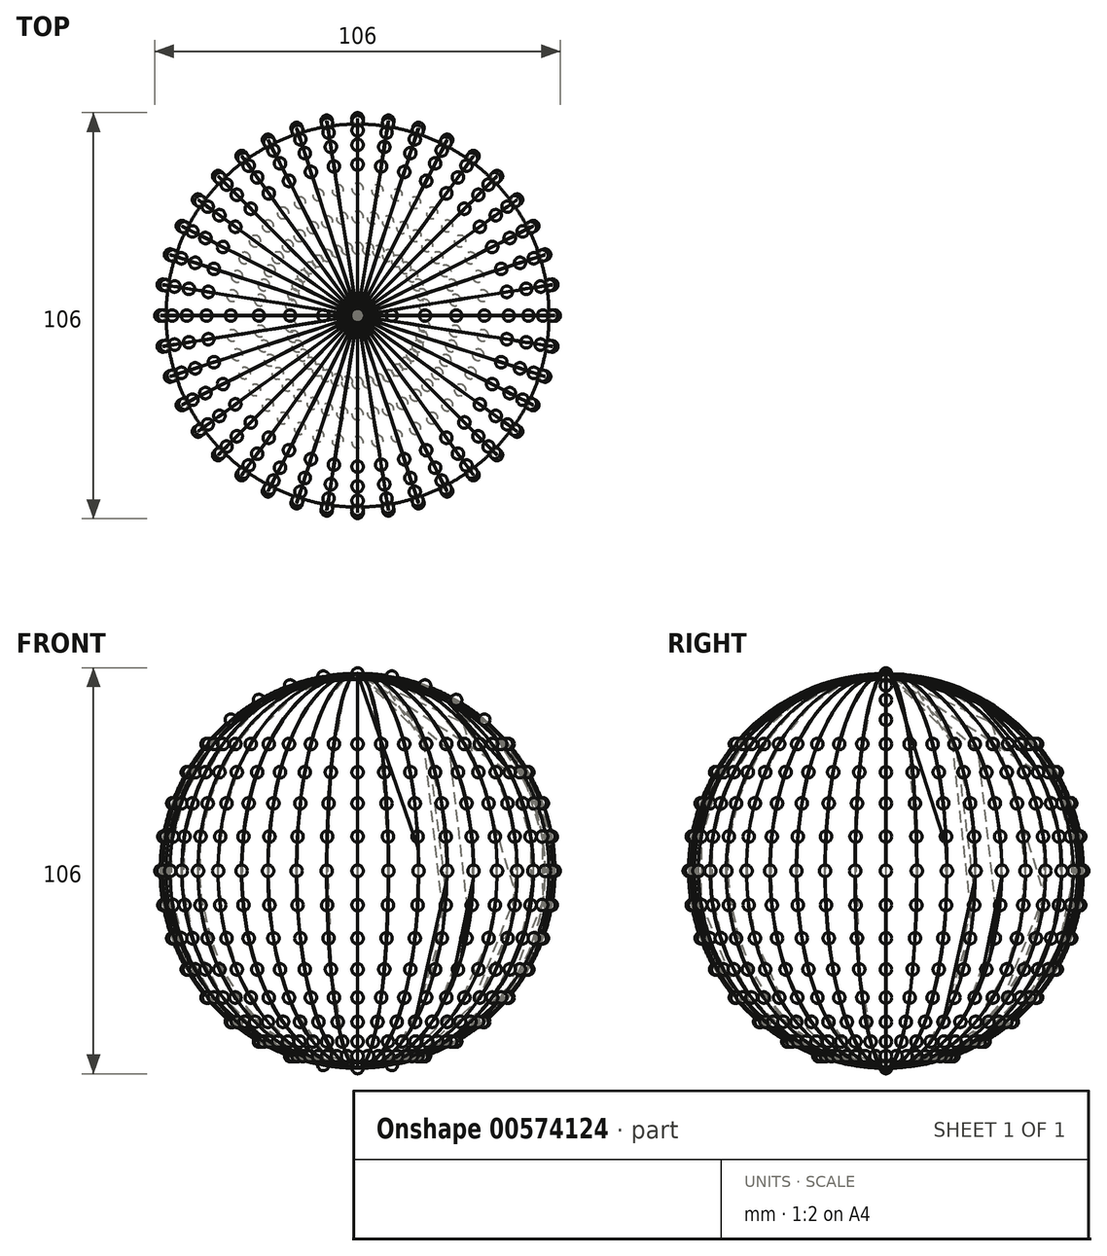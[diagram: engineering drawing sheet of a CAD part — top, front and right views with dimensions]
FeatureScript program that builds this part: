
annotation { "Feature Type Name" : "Feature", "Feature Type Description" : "" }
export const myFeature = defineFeature(function(context is Context, id is Id, definition is map)
    precondition{}
    {
        {
            var Q0;
            Q0=qCreatedBy(makeId("Front.planeOp"),FACE);
            var sketch = newSketch(context, id + "F0", { "sketchPlane" : qUnion([Q0])});
            skArc(sketch, "E0", {"start": v(0, -50) * mm, "mid": v(50, 0) * mm, "end": v(0, 50) * mm});
            skCircle(sketch, "E1", {"center": v(0, 0) * mm, "radius": 51.5 * mm});
            skLineSegment(sketch, "E2", {"start": v(0, 50) * mm, "end": v(0, -50) * mm});
            skSolve(sketch);
        }
        {
            var Q0;
            Q0=makeQuery(id+"F0.imprint","IMPRINT",FACE,{"disambiguationData":[TD([[makeQuery(id+"F0.imprint","IMPRINT",EDGE,{"derivedFrom":sQuery(id+"F0.wireOp",EDGE,"E0")}),1.0]])]});
            var Q1;
            Q1=sQuery(id+"F0.wireOp",EDGE,"E2");
            revolve(context, id + "F1", {"entities" : qUnion([Q0]), "axis" : qUnion([Q1]), "revolveType" : RevolveType.FULL});
        }
        {
            var Q0;
            Q0=qCreatedBy(makeId("Right.planeOp"),FACE);
            var sketch = newSketch(context, id + "F2", { "sketchPlane" : qUnion([Q0])});
            skLineSegment(sketch, "E3.0", {"start": v(0, -51.5) * mm, "end": v(0, 51.5) * mm, "construction": true});
            skCircle(sketch, "E4", {"center": v(0, 51.5) * mm, "radius": 0.05 * mm});
            skSolve(sketch);
        }
        {
            var Q0;
            Q0=makeQuery(id+"F2.imprint","IMPRINT",FACE,{"disambiguationData":[TD([[makeQuery(id+"F2.imprint","IMPRINT",EDGE,{"derivedFrom":sQuery(id+"F2.wireOp",EDGE,"E4")}),1.0]])]});
            var Q1;
            Q1=sQuery(id+"F0.wireOp",EDGE,"E1");
            sweep(context, id + "F3", {"profiles" : qUnion([Q0]), "path" : qUnion([Q1])});
        }
        {
            var Q0;
            Q0=qCreatedBy(makeId("Front.planeOp"),FACE);
            var sketch = newSketch(context, id + "F4", { "sketchPlane" : qUnion([Q0])});
            skArc(sketch, "E5", {"start": v(0, 50) * mm, "mid": v(1.5, 51.5) * mm, "end": v(0, 53) * mm});
            skLineSegment(sketch, "E6", {"start": v(0, 53) * mm, "end": v(0, 50) * mm});
            skSolve(sketch);
        }
        {
            var Q0;
            Q0 = qSketchRegion(id + "F4", true);
            var Q1;
            Q1=sQuery(id+"F4.wireOp",EDGE,"E6");
            revolve(context, id + "F5", {"entities" : qUnion([Q0]), "axis" : qUnion([Q1]), "revolveType" : RevolveType.FULL});
        }
        {
            var Q0;
            Q0=makeQuery(id+"F5.opRevolve","SWEPT_BODY",BODY,{"disambiguationData":[OSD([sQuery(id+"F4.wireOp",EDGE,"E5"),sQuery(id+"F4.wireOp",EDGE,"E6")])]});
            var Q1;
            Q1=sQuery(id+"F0.wireOp",EDGE,"E1");
            circularPattern(context, id + "F6", {"entities" : qUnion([Q0]), "axis" : qUnion([Q1]), "angle" : 360 * degree, "instanceCount" : 36, "equalSpace" : true});
        }
        {
            var Q0;
            Q0=makeQuery(id+"F6.opPattern","COPY",BODY,{"derivedFrom":makeQuery(id+"F5.opRevolve","SWEPT_BODY",BODY,{"disambiguationData":[OSD([sQuery(id+"F4.wireOp",EDGE,"E5"),sQuery(id+"F4.wireOp",EDGE,"E6")])]}),"instanceName":"27"});
            var Q1;
            Q1=makeQuery(id+"F3.opSweep","SWEPT_BODY",BODY,{"disambiguationData":[OSD([sQuery(id+"F0.wireOp",EDGE,"E1"),sQuery(id+"F2.wireOp",EDGE,"E4")])]});
            var Q2;
            Q2=makeQuery(id+"F6.opPattern","COPY",BODY,{"derivedFrom":makeQuery(id+"F5.opRevolve","SWEPT_BODY",BODY,{"disambiguationData":[OSD([sQuery(id+"F4.wireOp",EDGE,"E5"),sQuery(id+"F4.wireOp",EDGE,"E6")])]}),"instanceName":"26"});
            var Q3;
            Q3=makeQuery(id+"F6.opPattern","COPY",BODY,{"derivedFrom":makeQuery(id+"F5.opRevolve","SWEPT_BODY",BODY,{"disambiguationData":[OSD([sQuery(id+"F4.wireOp",EDGE,"E5"),sQuery(id+"F4.wireOp",EDGE,"E6")])]}),"instanceName":"25"});
            var Q4;
            Q4=makeQuery(id+"F6.opPattern","COPY",BODY,{"derivedFrom":makeQuery(id+"F5.opRevolve","SWEPT_BODY",BODY,{"disambiguationData":[OSD([sQuery(id+"F4.wireOp",EDGE,"E5"),sQuery(id+"F4.wireOp",EDGE,"E6")])]}),"instanceName":"28"});
            var Q5;
            Q5=makeQuery(id+"F6.opPattern","COPY",BODY,{"derivedFrom":makeQuery(id+"F5.opRevolve","SWEPT_BODY",BODY,{"disambiguationData":[OSD([sQuery(id+"F4.wireOp",EDGE,"E5"),sQuery(id+"F4.wireOp",EDGE,"E6")])]}),"instanceName":"29"});
            var Q6;
            Q6=makeQuery(id+"F6.opPattern","COPY",BODY,{"derivedFrom":makeQuery(id+"F5.opRevolve","SWEPT_BODY",BODY,{"disambiguationData":[OSD([sQuery(id+"F4.wireOp",EDGE,"E5"),sQuery(id+"F4.wireOp",EDGE,"E6")])]}),"instanceName":"30"});
            var Q7;
            Q7=makeQuery(id+"F6.opPattern","COPY",BODY,{"derivedFrom":makeQuery(id+"F5.opRevolve","SWEPT_BODY",BODY,{"disambiguationData":[OSD([sQuery(id+"F4.wireOp",EDGE,"E5"),sQuery(id+"F4.wireOp",EDGE,"E6")])]}),"instanceName":"31"});
            var Q8;
            Q8=makeQuery(id+"F6.opPattern","COPY",BODY,{"derivedFrom":makeQuery(id+"F5.opRevolve","SWEPT_BODY",BODY,{"disambiguationData":[OSD([sQuery(id+"F4.wireOp",EDGE,"E5"),sQuery(id+"F4.wireOp",EDGE,"E6")])]}),"instanceName":"24"});
            var Q9;
            Q9=makeQuery(id+"F6.opPattern","COPY",BODY,{"derivedFrom":makeQuery(id+"F5.opRevolve","SWEPT_BODY",BODY,{"disambiguationData":[OSD([sQuery(id+"F4.wireOp",EDGE,"E5"),sQuery(id+"F4.wireOp",EDGE,"E6")])]}),"instanceName":"23"});
            var Q10;
            Q10=makeQuery(id+"F6.opPattern","COPY",BODY,{"derivedFrom":makeQuery(id+"F5.opRevolve","SWEPT_BODY",BODY,{"disambiguationData":[OSD([sQuery(id+"F4.wireOp",EDGE,"E5"),sQuery(id+"F4.wireOp",EDGE,"E6")])]}),"instanceName":"22"});
            var Q11;
            Q11=makeQuery(id+"F6.opPattern","COPY",BODY,{"derivedFrom":makeQuery(id+"F5.opRevolve","SWEPT_BODY",BODY,{"disambiguationData":[OSD([sQuery(id+"F4.wireOp",EDGE,"E5"),sQuery(id+"F4.wireOp",EDGE,"E6")])]}),"instanceName":"21"});
            var Q12;
            Q12=makeQuery(id+"F6.opPattern","COPY",BODY,{"derivedFrom":makeQuery(id+"F5.opRevolve","SWEPT_BODY",BODY,{"disambiguationData":[OSD([sQuery(id+"F4.wireOp",EDGE,"E5"),sQuery(id+"F4.wireOp",EDGE,"E6")])]}),"instanceName":"20"});
            var Q13;
            Q13=sQuery(id+"F2.wireOp",EDGE,"E3.0");
            circularPattern(context, id + "F7", {"entities" : qUnion([Q0, Q1, Q2, Q3, Q4, Q5, Q6, Q7, Q8, Q9, Q10, Q11, Q12]), "axis" : qUnion([Q13]), "angle" : 360 * degree, "instanceCount" : 40, "equalSpace" : true});
        }
        {
            var Q0;
            Q0=qCreatedBy(makeId("Front.planeOp"),FACE);
            var sketch = newSketch(context, id + "F8", { "sketchPlane" : qUnion([Q0])});
            skCircle(sketch, "E7", {"center": v(0, 0) * mm, "radius": 1.5 * mm, "construction": true});
            skCircle(sketch, "E8", {"center": v(7.93, -8.94) * mm, "radius": 1.5 * mm, "construction": true});
            skCircle(sketch, "E9", {"center": v(7.93, 8.94) * mm, "radius": 1.5 * mm, "construction": true});
            skLineSegment(sketch, "E10", {"start": v(0, 0) * mm, "end": v(7.93, 8.94) * mm, "construction": true});
            skLineSegment(sketch, "E11", {"start": v(0, 0) * mm, "end": v(7.93, -8.94) * mm, "construction": true});
            skCircle(sketch, "E12", {"center": v(-7.93, -8.94) * mm, "radius": 1.5 * mm});
            skCircle(sketch, "E13", {"center": v(-7.93, 8.94) * mm, "radius": 1.5 * mm});
            skLineSegment(sketch, "E14", {"start": v(0, 0) * mm, "end": v(-7.93, 8.94) * mm, "construction": true});
            skCircle(sketch, "E15", {"center": v(-15.67, 8.94) * mm, "radius": 1.5 * mm});
            skCircle(sketch, "E16", {"center": v(-14.95, 17.61) * mm, "radius": 1.5 * mm});
            skCircle(sketch, "E17", {"center": v(-7.57, 17.61) * mm, "radius": 1.5 * mm});
            skCircle(sketch, "E18", {"center": v(-6.98, 25.75) * mm, "radius": 1.5 * mm});
            skCircle(sketch, "E19", {"center": v(-13.78, 25.75) * mm, "radius": 1.5 * mm});
            skCircle(sketch, "E20", {"center": v(-6.17, 33.1) * mm, "radius": 1.5 * mm});
            skCircle(sketch, "E21", {"center": v(-12.2, 33.1) * mm, "radius": 1.5 * mm});
            skCircle(sketch, "E22", {"center": v(-17.91, 33.1) * mm, "radius": 1.5 * mm});
            skCircle(sketch, "E23", {"center": v(-23.19, 33.1) * mm, "radius": 1.5 * mm});
            skCircle(sketch, "E24", {"center": v(-27.9, 33.1) * mm, "radius": 1.5 * mm});
            skCircle(sketch, "E25", {"center": v(-31.92, 33.1) * mm, "radius": 1.5 * mm});
            skCircle(sketch, "E26", {"center": v(-35.15, 33.1) * mm, "radius": 1.5 * mm});
            skCircle(sketch, "E27", {"center": v(-36.08, 25.75) * mm, "radius": 1.5 * mm});
            skCircle(sketch, "E28", {"center": v(-31.54, 25.75) * mm, "radius": 1.5 * mm});
            skCircle(sketch, "E29", {"center": v(-26.22, 25.75) * mm, "radius": 1.5 * mm});
            skLineSegment(sketch, "E30.0", {"start": v(0, -51.5) * mm, "end": v(0, 51.5) * mm});
            skCircle(sketch, "E31", {"center": v(6.17, 33.1) * mm, "radius": 1.5 * mm});
            skCircle(sketch, "E32", {"center": v(6.98, 25.75) * mm, "radius": 1.5 * mm});
            skCircle(sketch, "E33", {"center": v(0, 25.75) * mm, "radius": 1.5 * mm});
            skCircle(sketch, "E34", {"center": v(17.91, 33.1) * mm, "radius": 1.5 * mm});
            skCircle(sketch, "E35", {"center": v(27.9, 33.1) * mm, "radius": 1.5 * mm});
            skCircle(sketch, "E36", {"center": v(35.15, 33.1) * mm, "radius": 1.5 * mm});
            skCircle(sketch, "E37", {"center": v(0, 0) * mm, "radius": 50 * mm});
            skCircle(sketch, "E38", {"center": v(39.74, 25.75) * mm, "radius": 1.5 * mm});
            skCircle(sketch, "E39", {"center": v(31.54, 25.75) * mm, "radius": 1.5 * mm});
            skCircle(sketch, "E40", {"center": v(20.25, 25.75) * mm, "radius": 1.5 * mm});
            skCircle(sketch, "E41", {"center": v(7.57, 17.61) * mm, "radius": 1.5 * mm});
            skCircle(sketch, "E42", {"center": v(14.95, 17.61) * mm, "radius": 1.5 * mm});
            skCircle(sketch, "E43", {"center": v(21.97, 17.61) * mm, "radius": 1.5 * mm});
            skCircle(sketch, "E44", {"center": v(34.22, 17.61) * mm, "radius": 1.5 * mm});
            skCircle(sketch, "E45", {"center": v(39.15, 17.61) * mm, "radius": 1.5 * mm});
            skCircle(sketch, "E46", {"center": v(46.03, 17.61) * mm, "radius": 1.5 * mm});
            skCircle(sketch, "E47", {"center": v(45.19, 8.94) * mm, "radius": 1.5 * mm});
            skCircle(sketch, "E48", {"center": v(35.86, 8.94) * mm, "radius": 1.5 * mm});
            skCircle(sketch, "E49", {"center": v(15.67, 8.94) * mm, "radius": 1.5 * mm});
            skCircle(sketch, "E50", {"center": v(23.38, 0) * mm, "radius": 1.5 * mm});
            skCircle(sketch, "E51", {"center": v(30.27, 0) * mm, "radius": 1.5 * mm});
            skCircle(sketch, "E52", {"center": v(48.98, 0) * mm, "radius": 1.5 * mm});
            skCircle(sketch, "E53", {"center": v(48.24, -8.94) * mm, "radius": 1.5 * mm});
            skCircle(sketch, "E54", {"center": v(41.03, -8.94) * mm, "radius": 1.5 * mm});
            skCircle(sketch, "E55", {"center": v(29.81, -8.94) * mm, "radius": 1.5 * mm});
            skCircle(sketch, "E56", {"center": v(0, -8.94) * mm, "radius": 1.5 * mm});
            skCircle(sketch, "E57", {"center": v(-15.67, -8.94) * mm, "radius": 1.5 * mm});
            skCircle(sketch, "E58", {"center": v(-28.45, 17.61) * mm, "radius": 1.5 * mm});
            skCircle(sketch, "E59", {"center": v(-15.91, 0) * mm, "radius": 1.5 * mm});
            skCircle(sketch, "E60", {"center": v(-45.89, 0) * mm, "radius": 1.5 * mm});
            skCircle(sketch, "E61", {"center": v(-45.19, 8.94) * mm, "radius": 1.5 * mm});
            skCircle(sketch, "E62", {"center": v(-46.03, -17.61) * mm, "radius": 1.5 * mm});
            skCircle(sketch, "E63", {"center": v(-43.12, -17.61) * mm, "radius": 1.5 * mm});
            skCircle(sketch, "E64", {"center": v(-21.97, -17.61) * mm, "radius": 1.5 * mm});
            skCircle(sketch, "E65", {"center": v(-7.57, -17.61) * mm, "radius": 1.5 * mm});
            skCircle(sketch, "E66", {"center": v(-34.22, -17.61) * mm, "radius": 1.5 * mm});
            skCircle(sketch, "E67", {"center": v(-29.81, -8.94) * mm, "radius": 1.5 * mm});
            skCircle(sketch, "E68", {"center": v(-41.03, -8.94) * mm, "radius": 1.5 * mm});
            skCircle(sketch, "E69", {"center": v(-45.19, -8.94) * mm, "radius": 1.5 * mm});
            skCircle(sketch, "E70", {"center": v(-41.66, 0) * mm, "radius": 1.5 * mm});
            skCircle(sketch, "E71", {"center": v(-36.42, 0) * mm, "radius": 1.5 * mm});
            skCircle(sketch, "E72", {"center": v(-30.27, 0) * mm, "radius": 1.5 * mm});
            skCircle(sketch, "E73", {"center": v(-23.38, 0) * mm, "radius": 1.5 * mm});
            skCircle(sketch, "E74", {"center": v(-23.03, 8.94) * mm, "radius": 1.5 * mm});
            skCircle(sketch, "E75", {"center": v(-29.81, 8.94) * mm, "radius": 1.5 * mm});
            skCircle(sketch, "E76", {"center": v(-41.03, 8.94) * mm, "radius": 1.5 * mm});
            skCircle(sketch, "E77", {"center": v(-42.42, -25.75) * mm, "radius": 1.5 * mm});
            skCircle(sketch, "E78", {"center": v(-39.74, -25.75) * mm, "radius": 1.5 * mm});
            skCircle(sketch, "E79", {"center": v(-26.22, -25.75) * mm, "radius": 1.5 * mm});
            skCircle(sketch, "E80", {"center": v(-6.98, -25.75) * mm, "radius": 1.5 * mm});
            skCircle(sketch, "E81", {"center": v(0, -17.61) * mm, "radius": 1.5 * mm});
            skCircle(sketch, "E82", {"center": v(15.67, -8.94) * mm, "radius": 1.5 * mm});
            skCircle(sketch, "E83", {"center": v(15.91, 0) * mm, "radius": 1.5 * mm});
            skCircle(sketch, "E84", {"center": v(8.06, 0) * mm, "radius": 1.5 * mm});
            skCircle(sketch, "E85", {"center": v(45.89, 0) * mm, "radius": 1.5 * mm});
            skCircle(sketch, "E86", {"center": v(41.66, 0) * mm, "radius": 1.5 * mm});
            skCircle(sketch, "E87", {"center": v(36.42, 0) * mm, "radius": 1.5 * mm});
            skCircle(sketch, "E88", {"center": v(29.81, 8.94) * mm, "radius": 1.5 * mm});
            skCircle(sketch, "E89", {"center": v(23.03, 8.94) * mm, "radius": 1.5 * mm});
            skCircle(sketch, "E90", {"center": v(28.45, 17.61) * mm, "radius": 1.5 * mm});
            skCircle(sketch, "E91", {"center": v(26.22, 25.75) * mm, "radius": 1.5 * mm});
            skCircle(sketch, "E92", {"center": v(23.19, 33.1) * mm, "radius": 1.5 * mm});
            skCircle(sketch, "E93", {"center": v(21.97, -17.61) * mm, "radius": 1.5 * mm});
            skCircle(sketch, "E94", {"center": v(7.57, -17.61) * mm, "radius": 1.5 * mm});
            skCircle(sketch, "E95", {"center": v(0, -25.75) * mm, "radius": 1.5 * mm});
            skCircle(sketch, "E96", {"center": v(6.98, -25.75) * mm, "radius": 1.5 * mm});
            skCircle(sketch, "E97", {"center": v(26.22, -25.75) * mm, "radius": 1.5 * mm});
            skCircle(sketch, "E98", {"center": v(20.25, -25.75) * mm, "radius": 1.5 * mm});
            skCircle(sketch, "E99", {"center": v(13.78, -25.75) * mm, "radius": 1.5 * mm});
            skCircle(sketch, "E100", {"center": v(14.95, -17.61) * mm, "radius": 1.5 * mm});
            skCircle(sketch, "E101", {"center": v(0, 33.1) * mm, "radius": 1.5 * mm});
            skCircle(sketch, "E102", {"center": v(12.2, 33.1) * mm, "radius": 1.5 * mm});
            skCircle(sketch, "E103", {"center": v(13.78, 25.75) * mm, "radius": 1.5 * mm});
            skCircle(sketch, "E104", {"center": v(31.92, 33.1) * mm, "radius": 1.5 * mm});
            skCircle(sketch, "E105", {"center": v(37.52, 33.1) * mm, "radius": 1.5 * mm});
            skCircle(sketch, "E106", {"center": v(36.08, 25.75) * mm, "radius": 1.5 * mm});
            skCircle(sketch, "E107", {"center": v(-20.25, 25.75) * mm, "radius": 1.5 * mm});
            skCircle(sketch, "E108", {"center": v(-21.97, 17.61) * mm, "radius": 1.5 * mm});
            skCircle(sketch, "E109", {"center": v(-34.22, 17.61) * mm, "radius": 1.5 * mm});
            skCircle(sketch, "E110", {"center": v(-39.15, 17.61) * mm, "radius": 1.5 * mm});
            skCircle(sketch, "E111", {"center": v(28.45, -17.61) * mm, "radius": 1.5 * mm});
            skCircle(sketch, "E112", {"center": v(45.19, -8.94) * mm, "radius": 1.5 * mm});
            skCircle(sketch, "E113", {"center": v(34.22, -17.61) * mm, "radius": 1.5 * mm});
            skCircle(sketch, "E114", {"center": v(35.86, -8.94) * mm, "radius": 1.5 * mm});
            skCircle(sketch, "E115", {"center": v(39.15, -17.61) * mm, "radius": 1.5 * mm});
            skCircle(sketch, "E116", {"center": v(43.12, -17.61) * mm, "radius": 1.5 * mm});
            skCircle(sketch, "E117", {"center": v(46.03, -17.61) * mm, "radius": 1.5 * mm});
            skCircle(sketch, "E118", {"center": v(39.74, -25.75) * mm, "radius": 1.5 * mm});
            skCircle(sketch, "E119", {"center": v(42.42, -25.75) * mm, "radius": 1.5 * mm});
            skCircle(sketch, "E120", {"center": v(31.54, -25.75) * mm, "radius": 1.5 * mm});
            skCircle(sketch, "E121", {"center": v(27.9, -33.1) * mm, "radius": 1.5 * mm});
            skCircle(sketch, "E122", {"center": v(31.92, -33.1) * mm, "radius": 1.5 * mm});
            skCircle(sketch, "E123", {"center": v(23.19, -33.1) * mm, "radius": 1.5 * mm});
            skCircle(sketch, "E124", {"center": v(17.91, -33.1) * mm, "radius": 1.5 * mm});
            skCircle(sketch, "E125", {"center": v(12.2, -33.1) * mm, "radius": 1.5 * mm});
            skCircle(sketch, "E126", {"center": v(0, -33.1) * mm, "radius": 1.5 * mm});
            skCircle(sketch, "E127", {"center": v(-12.2, -33.1) * mm, "radius": 1.5 * mm});
            skCircle(sketch, "E128", {"center": v(-17.91, -33.1) * mm, "radius": 1.5 * mm});
            skCircle(sketch, "E129", {"center": v(-31.54, -25.75) * mm, "radius": 1.5 * mm});
            skCircle(sketch, "E130", {"center": v(-36.08, -25.75) * mm, "radius": 1.5 * mm});
            skCircle(sketch, "E131", {"center": v(-37.52, -33.1) * mm, "radius": 1.5 * mm});
            skLineSegment(sketch, "E132", {"start": v(0, 0) * mm, "end": v(-7.93, -8.94) * mm, "construction": true});
            skSolve(sketch);
        }
        {
            var Q0;
            Q0=sQuery(id+"F8.wireOp",EDGE,"E10");
            cPlane(context, id + "F9", {"entities" : qUnion([Q0]), "cplaneType" : CPlaneType.LINE_ANGLE, "offset" : 25 * mm, "angle" : 0 * degree, "width" : 150 * mm, "height" : 150 * mm});
        }
        {
            var Q0;
            Q0=qCreatedBy(id+"F9.planeOp",FACE);
            var sketch = newSketch(context, id + "F10", { "sketchPlane" : qUnion([Q0])});
            skCircle(sketch, "E133", {"center": v(0, 0) * mm, "radius": 51.5 * mm});
            skSolve(sketch);
        }
        {
            var Q0;
            Q0=sQuery(id+"F8.wireOp",EDGE,"E14");
            var Q1;
            Q1=sQuery(id+"F8.wireOp",EDGE,"E30.0");
            cPlane(context, id + "F11", {"entities" : qUnion([Q0, Q1]), "cplaneType" : CPlaneType.LINE_ANGLE, "offset" : 25 * mm, "angle" : 60 * degree, "width" : 150 * mm, "height" : 150 * mm});
        }
    });
